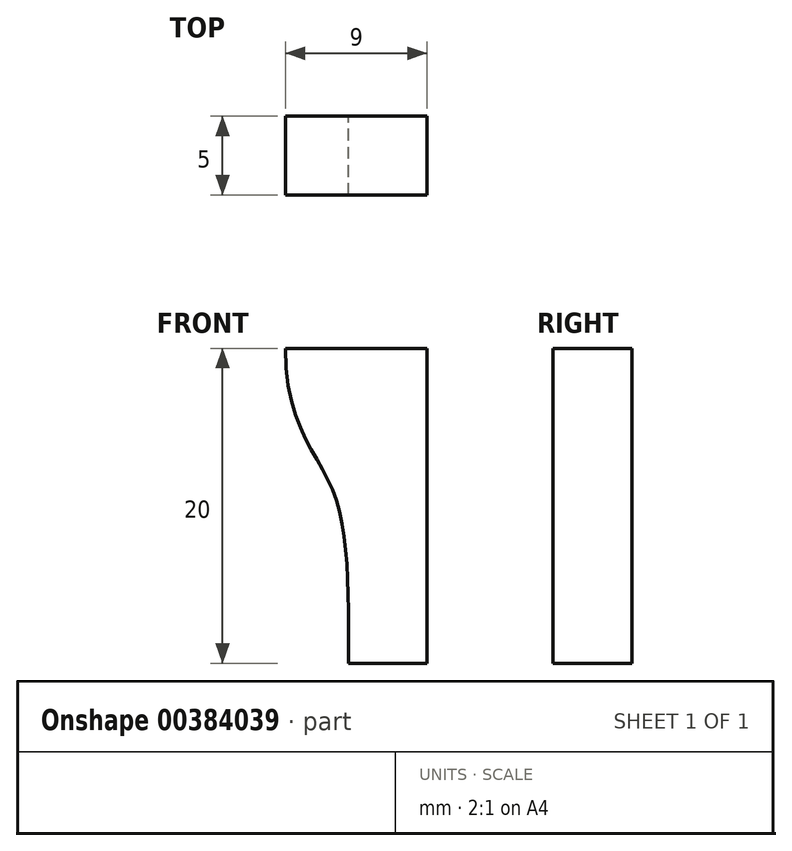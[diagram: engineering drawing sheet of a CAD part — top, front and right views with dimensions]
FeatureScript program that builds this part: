
annotation { "Feature Type Name" : "Feature", "Feature Type Description" : "" }
export const myFeature = defineFeature(function(context is Context, id is Id, definition is map)
    precondition{}
    {
        {
            var Q0;
            Q0=qCreatedBy(makeId("Front.planeOp"),FACE);
            var sketch = newSketch(context, id + "F0", { "sketchPlane" : qUnion([Q0])});
            skLineSegment(sketch, "E0", {"start": v(-5, 0) * mm, "end": v(0, 0) * mm});
            skLineSegment(sketch, "E1", {"start": v(0, 0) * mm, "end": v(0, 20) * mm});
            skLineSegment(sketch, "E2", {"start": v(0, 20) * mm, "end": v(-9, 20) * mm});
            skLineSegment(sketch, "E3", {"start": v(0, 11) * mm, "end": v(-6, 11) * mm, "construction": true});
            skFitSpline(sketch, "E4", {"points": [v(-9, 20) * mm, v(-6, 11) * mm, v(-5, 0) * mm], "startDerivative": vector(0, -30.47) * mm, "endDerivative": vector(0, -27.34) * mm});
            skSolve(sketch);
        }
        {
            var Q0;
            Q0 = qSketchRegion(id + "F0", true);
            extrude(context, id + "F1", {"entities" : qUnion([Q0]), "depth" : 5 * mm});
        }
    });
